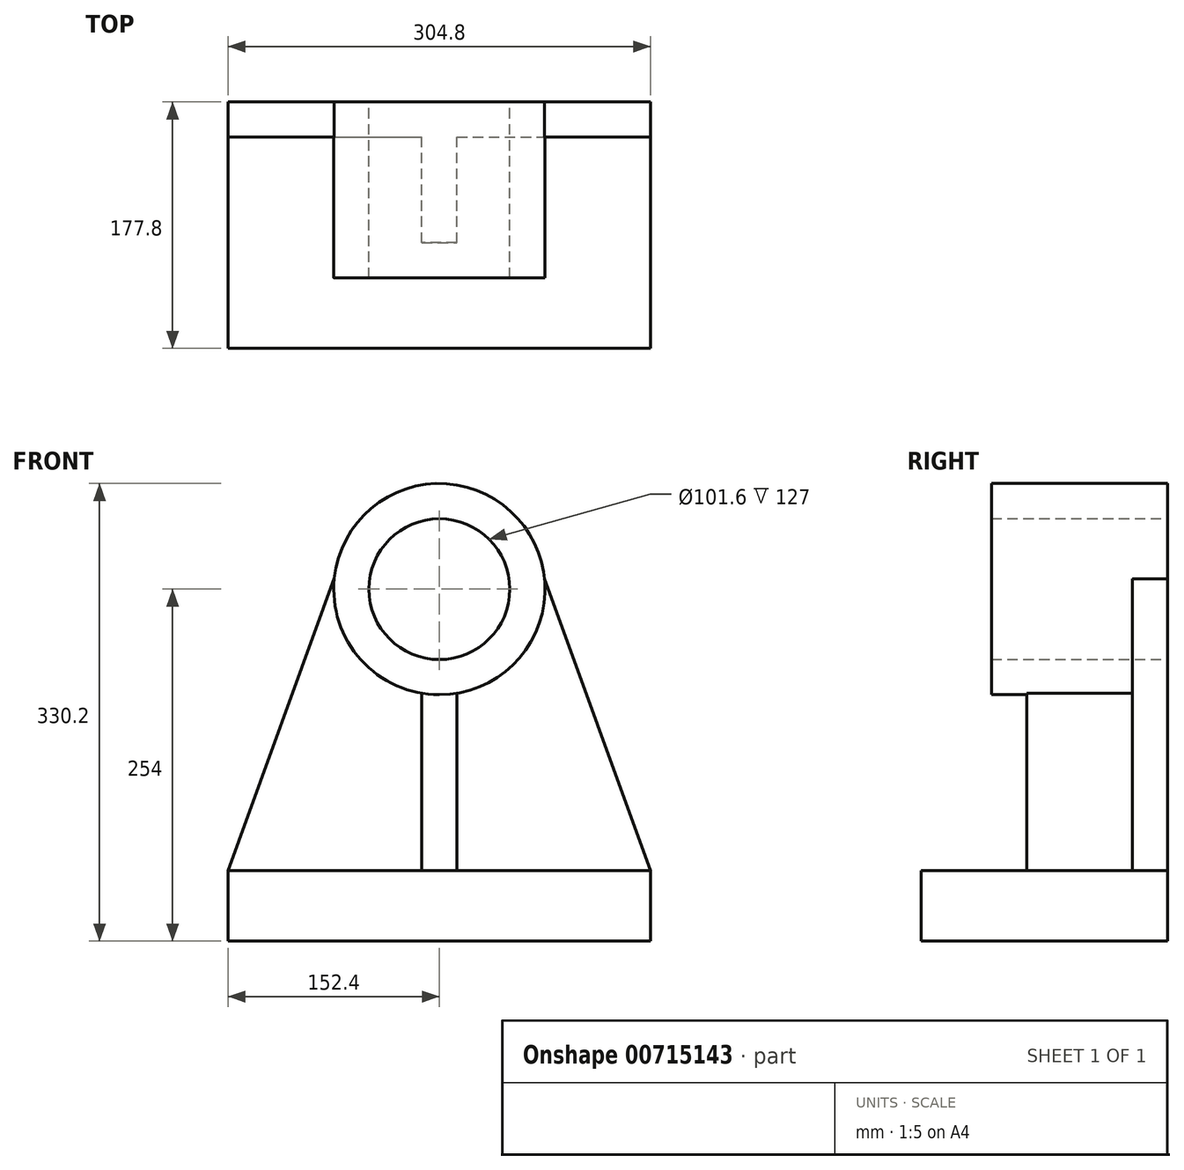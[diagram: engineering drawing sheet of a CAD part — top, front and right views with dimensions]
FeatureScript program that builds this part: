
annotation { "Feature Type Name" : "Feature", "Feature Type Description" : "" }
export const myFeature = defineFeature(function(context is Context, id is Id, definition is map)
    precondition{}
    {
        {
            var Q0;
            Q0=qCreatedBy(makeId("Front.planeOp"),FACE);
            var sketch = newSketch(context, id + "F0", { "sketchPlane" : qUnion([Q0])});
            skCircle(sketch, "E0", {"center": v(0, 0) * mm, "radius": 50.8 * mm});
            skCircle(sketch, "E1", {"center": v(0, 0) * mm, "radius": 76.2 * mm});
            skLineSegment(sketch, "E2", {"start": v(-12.7, -75.13) * mm, "end": v(-12.7, -203.2) * mm});
            skLineSegment(sketch, "E3", {"start": v(12.7, -75.13) * mm, "end": v(12.7, -203.2) * mm});
            skLineSegment(sketch, "E4", {"start": v(12.7, -203.2) * mm, "end": v(-12.7, -203.2) * mm});
            skLineSegment(sketch, "E5", {"start": v(-75.8, 7.77) * mm, "end": v(-152.4, -203.2) * mm});
            skLineSegment(sketch, "E6", {"start": v(75.84, 7.38) * mm, "end": v(152.4, -203.2) * mm});
            skPoint(sketch, "E7", {"position": v(0, -254) * mm});
            skLineSegment(sketch, "E8", {"start": v(0, 0) * mm, "end": v(0, -254) * mm, "construction": true});
            skLineSegment(sketch, "E9.bottom", {"start": v(-152.4, -203.2) * mm, "end": v(152.4, -203.2) * mm});
            skLineSegment(sketch, "E9.top", {"start": v(-152.4, -254) * mm, "end": v(152.4, -254) * mm});
            skLineSegment(sketch, "E9.left", {"start": v(-152.4, -203.2) * mm, "end": v(-152.4, -254) * mm});
            skLineSegment(sketch, "E9.right", {"start": v(152.4, -203.2) * mm, "end": v(152.4, -254) * mm});
            skSolve(sketch);
        }
        {
            var Q0;
            Q0=makeQuery(id+"F0.imprint","IMPRINT",FACE,{"disambiguationData":[TD([[makeQuery(id+"F0.imprint","IMPRINT",EDGE,{"derivedFrom":sQuery(id+"F0.wireOp",EDGE,"E0")}),-1.0]])]});
            extrude(context, id + "F1", {"entities" : qUnion([Q0]), "depth" : 127 * mm, "offsetDistance" : 25.4 * mm});
        }
        {
            var Q0;
            {var subQ0=sQuery(id+"F0.wireOp",EDGE,"E2");Q0=makeQuery(id+"F0.imprint","IMPRINT",FACE,{"disambiguationData":[TD([[makeQuery(id+"F0.imprint","IMPRINT",EDGE,{"derivedFrom":subQ0}),1.0]])]});}
            extrude(context, id + "F2", {"entities" : qUnion([Q0]), "operationType" : NewBodyOperationType.ADD, "depth" : 101.6 * mm, "offsetDistance" : 25.4 * mm});
        }
        {
            var Q0;
            {var subQ0=sQuery(id+"F0.wireOp",EDGE,"E2");Q0=makeQuery(id+"F0.imprint","IMPRINT",FACE,{"disambiguationData":[TD([[makeQuery(id+"F0.imprint","IMPRINT",EDGE,{"derivedFrom":subQ0}),-1.0]])]});}
            var Q1;
            {var subQ0=sQuery(id+"F0.wireOp",EDGE,"E3");Q1=makeQuery(id+"F0.imprint","IMPRINT",FACE,{"disambiguationData":[TD([[makeQuery(id+"F0.imprint","IMPRINT",EDGE,{"derivedFrom":subQ0}),1.0]])]});}
            extrude(context, id + "F3", {"entities" : qUnion([Q0, Q1]), "operationType" : NewBodyOperationType.ADD, "depth" : 25.4 * mm, "offsetDistance" : 25.4 * mm});
        }
        {
            var Q0;
            Q0=makeQuery(id+"F0.imprint","IMPRINT",FACE,{"disambiguationData":[TD([[makeQuery(id+"F0.imprint","IMPRINT",EDGE,{"derivedFrom":sQuery(id+"F0.wireOp",EDGE,"E9.top")}),1.0]])]});
            extrude(context, id + "F4", {"entities" : qUnion([Q0]), "operationType" : NewBodyOperationType.ADD, "depth" : 25.4 * mm, "offsetDistance" : 25.4 * mm});
        }
        {
            var Q0;
            {var subQ0=sQuery(id+"F0.wireOp",EDGE,"E9.bottom");var subQ1=sQuery(id+"F0.wireOp",EDGE,"E1");Q0=makeQuery(id+"F4.boolean.opBoolean","MERGE",FACE,{"derivedFrom":[makeQuery(id+"F3.opExtrude","CAP_FACE",FACE,{"disambiguationData":[OSD([subQ1,sQuery(id+"F0.wireOp",EDGE,"E2"),sQuery(id+"F0.wireOp",EDGE,"E5"),subQ0])],"isStart":false}),makeQuery(id+"F3.opExtrude","CAP_FACE",FACE,{"disambiguationData":[OSD([subQ1,sQuery(id+"F0.wireOp",EDGE,"E3"),sQuery(id+"F0.wireOp",EDGE,"E6"),subQ0])],"isStart":false}),makeQuery(id+"F4.opExtrude","CAP_FACE",FACE,{"disambiguationData":[OSD([subQ0,sQuery(id+"F0.wireOp",EDGE,"E9.top"),sQuery(id+"F0.wireOp",EDGE,"E9.left"),sQuery(id+"F0.wireOp",EDGE,"E9.right")])],"isStart":false})]});}
            var sketch = newSketch(context, id + "F5", { "sketchPlane" : qUnion([Q0])});
            skLineSegment(sketch, "E10.bottom", {"start": v(-152.4, -203.2) * mm, "end": v(152.4, -203.2) * mm});
            skLineSegment(sketch, "E10.top", {"start": v(-152.4, -254) * mm, "end": v(152.4, -254) * mm});
            skLineSegment(sketch, "E10.left", {"start": v(-152.4, -203.2) * mm, "end": v(-152.4, -254) * mm});
            skLineSegment(sketch, "E10.right", {"start": v(152.4, -203.2) * mm, "end": v(152.4, -254) * mm});
            skSolve(sketch);
        }
        {
            var Q0;
            Q0 = qSketchRegion(id + "F5", true);
            extrude(context, id + "F6", {"entities" : qUnion([Q0]), "operationType" : NewBodyOperationType.ADD, "depth" : 152.4 * mm, "offsetDistance" : 25.4 * mm});
        }
    });
